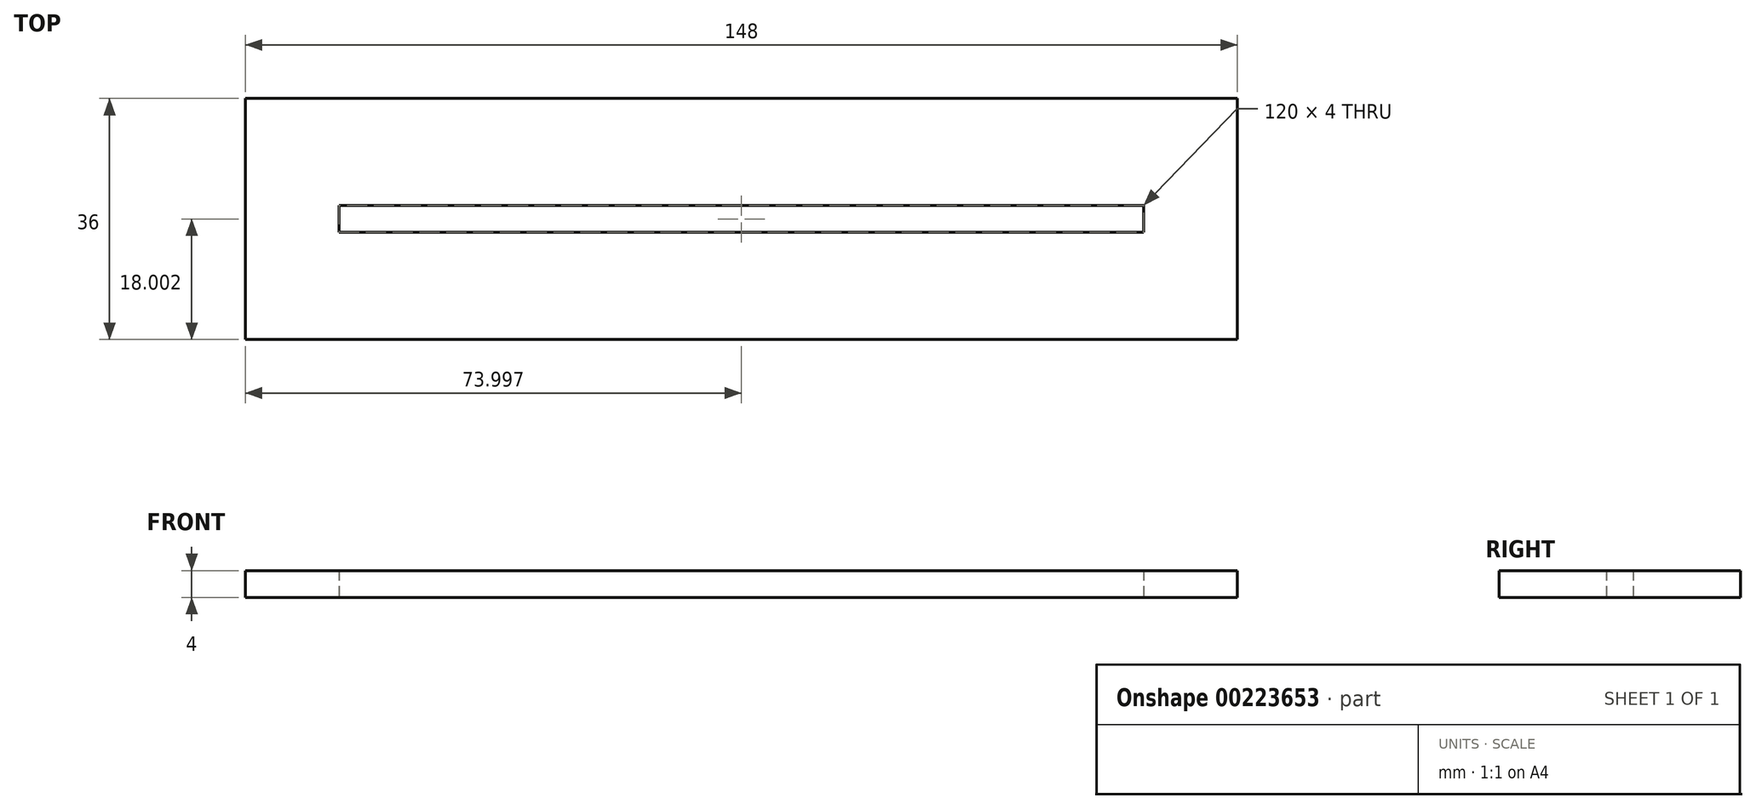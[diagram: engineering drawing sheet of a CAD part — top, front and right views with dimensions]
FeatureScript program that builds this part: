
annotation { "Feature Type Name" : "Feature", "Feature Type Description" : "" }
export const myFeature = defineFeature(function(context is Context, id is Id, definition is map)
    precondition{}
    {
        {
            var Q0;
            Q0=qCreatedBy(makeId("Top.planeOp"),FACE);
            var sketch = newSketch(context, id + "F0", { "sketchPlane" : qUnion([Q0])});
            skLineSegment(sketch, "E0", {"start": v(67.56, 14.06) * mm, "end": v(-80.44, 14.06) * mm});
            skLineSegment(sketch, "E1", {"start": v(-80.44, -21.94) * mm, "end": v(67.56, -21.94) * mm});
            skLineSegment(sketch, "E2", {"start": v(-80.44, 14.06) * mm, "end": v(-80.44, -1.94) * mm});
            skLineSegment(sketch, "E3", {"start": v(-80.44, -1.94) * mm, "end": v(-80.44, -5.94) * mm});
            skLineSegment(sketch, "E4", {"start": v(-80.44, -5.94) * mm, "end": v(-80.44, -21.94) * mm});
            skLineSegment(sketch, "E5", {"start": v(67.56, 14.06) * mm, "end": v(67.56, -1.94) * mm});
            skLineSegment(sketch, "E6", {"start": v(67.56, -1.94) * mm, "end": v(67.56, -5.94) * mm});
            skLineSegment(sketch, "E7", {"start": v(67.56, -5.94) * mm, "end": v(67.56, -21.94) * mm});
            skLineSegment(sketch, "E8", {"start": v(-66.44, -1.94) * mm, "end": v(53.56, -1.94) * mm});
            skLineSegment(sketch, "E9", {"start": v(53.56, -5.94) * mm, "end": v(-66.44, -5.94) * mm});
            skLineSegment(sketch, "E10", {"start": v(-66.44, -1.94) * mm, "end": v(-66.44, -5.94) * mm});
            skLineSegment(sketch, "E11", {"start": v(53.56, -1.94) * mm, "end": v(53.56, -5.94) * mm});
            skSolve(sketch);
        }
        {
            var Q0;
            Q0=makeQuery(id+"F0.imprint","IMPRINT",FACE,{"disambiguationData":[TD([[makeQuery(id+"F0.imprint","IMPRINT",EDGE,{"derivedFrom":sQuery(id+"F0.wireOp",EDGE,"E0")}),1.0]])]});
            extrude(context, id + "F1", {"entities" : qUnion([Q0]), "depth" : 4 * mm});
        }
    });
